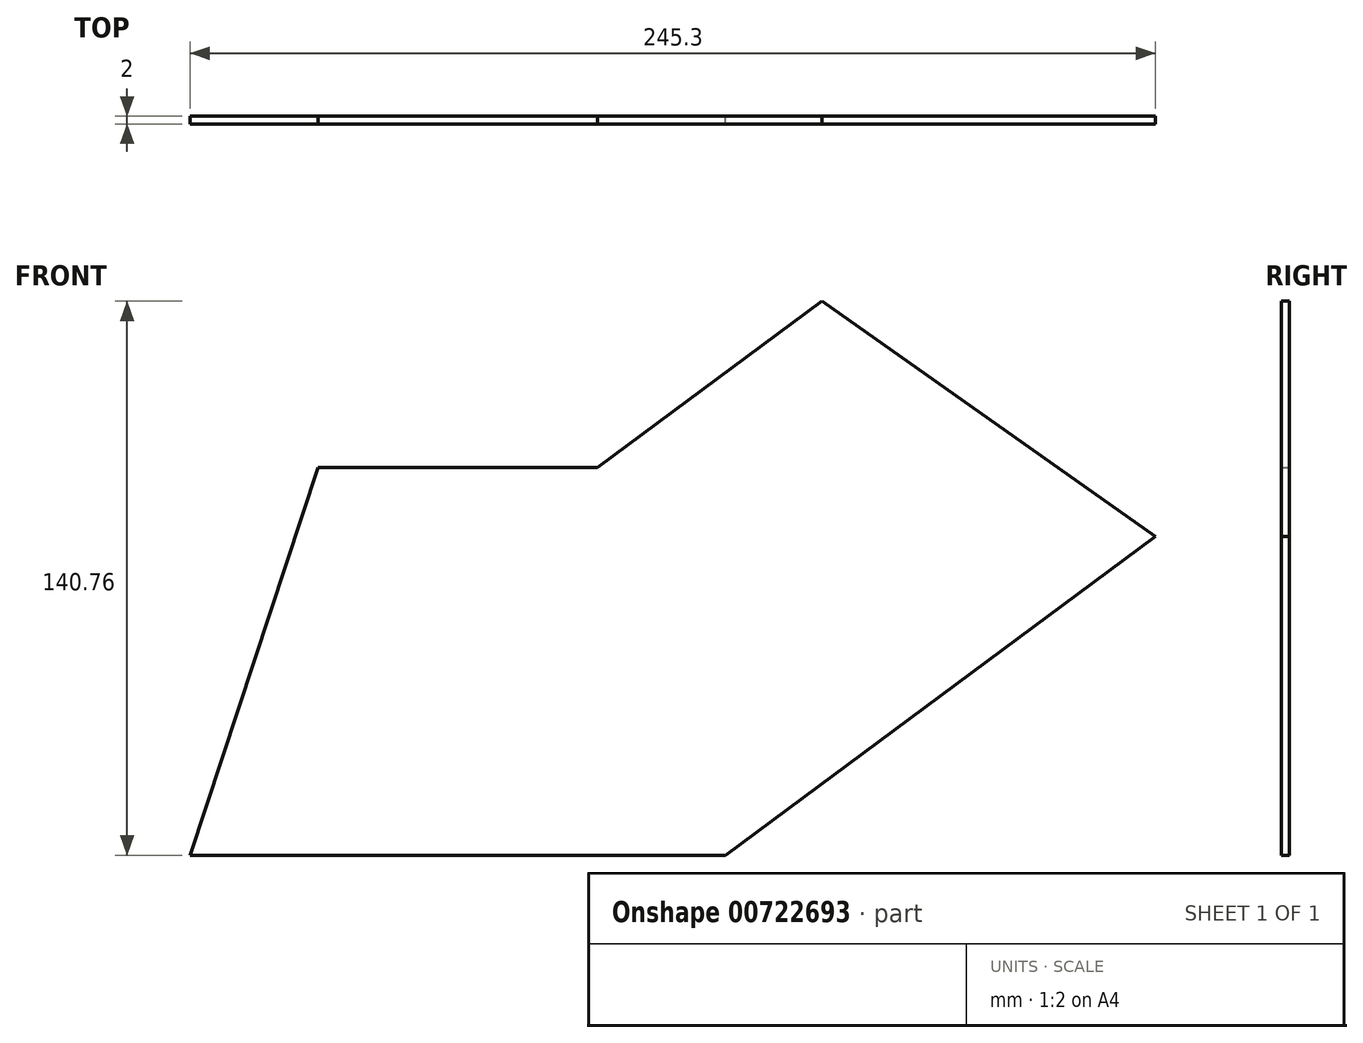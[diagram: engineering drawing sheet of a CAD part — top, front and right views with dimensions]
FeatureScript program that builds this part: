
annotation { "Feature Type Name" : "Feature", "Feature Type Description" : "" }
export const myFeature = defineFeature(function(context is Context, id is Id, definition is map)
    precondition{}
    {
        {
            var Q0;
            Q0=qCreatedBy(makeId("Front.planeOp"),FACE);
            var sketch = newSketch(context, id + "F0", { "sketchPlane" : qUnion([Q0])});
            skLineSegment(sketch, "E0", {"start": v(0, 44.41) * mm, "end": v(0, -46.44) * mm, "construction": true});
            skLineSegment(sketch, "E1", {"start": v(-35.5, 55.17) * mm, "end": v(35.5, 55.17) * mm});
            skLineSegment(sketch, "E2", {"start": v(-68, -43.33) * mm, "end": v(68, -43.33) * mm});
            skLineSegment(sketch, "E3", {"start": v(-68, -43.33) * mm, "end": v(-35.5, 55.17) * mm});
            skLineSegment(sketch, "E4", {"start": v(35.5, 55.17) * mm, "end": v(68, -43.33) * mm});
            skLineSegment(sketch, "E5", {"start": v(68, -43.33) * mm, "end": v(177.3, 37.6) * mm});
            skLineSegment(sketch, "E6", {"start": v(35.5, 55.17) * mm, "end": v(92.56, 97.43) * mm});
            skLineSegment(sketch, "E7", {"start": v(92.56, 97.43) * mm, "end": v(177.3, 37.6) * mm});
            skLineSegment(sketch, "E8", {"start": v(64.03, 76.3) * mm, "end": v(128.62, -10.92) * mm, "construction": true});
            skSolve(sketch);
        }
        {
            var Q0;
            Q0=makeQuery(id+"F0.imprint","IMPRINT",FACE,{"disambiguationData":[TD([[makeQuery(id+"F0.imprint","IMPRINT",EDGE,{"derivedFrom":sQuery(id+"F0.wireOp",EDGE,"E1")}),-1.0]])]});
            var Q1;
            Q1=makeQuery(id+"F0.imprint","IMPRINT",FACE,{"disambiguationData":[TD([[makeQuery(id+"F0.imprint","IMPRINT",EDGE,{"derivedFrom":sQuery(id+"F0.wireOp",EDGE,"E4")}),1.0]])]});
            extrude(context, id + "F1", {"entities" : qUnion([Q0, Q1]), "depth" : 2 * mm, "offsetDistance" : 25 * mm});
        }
    });
